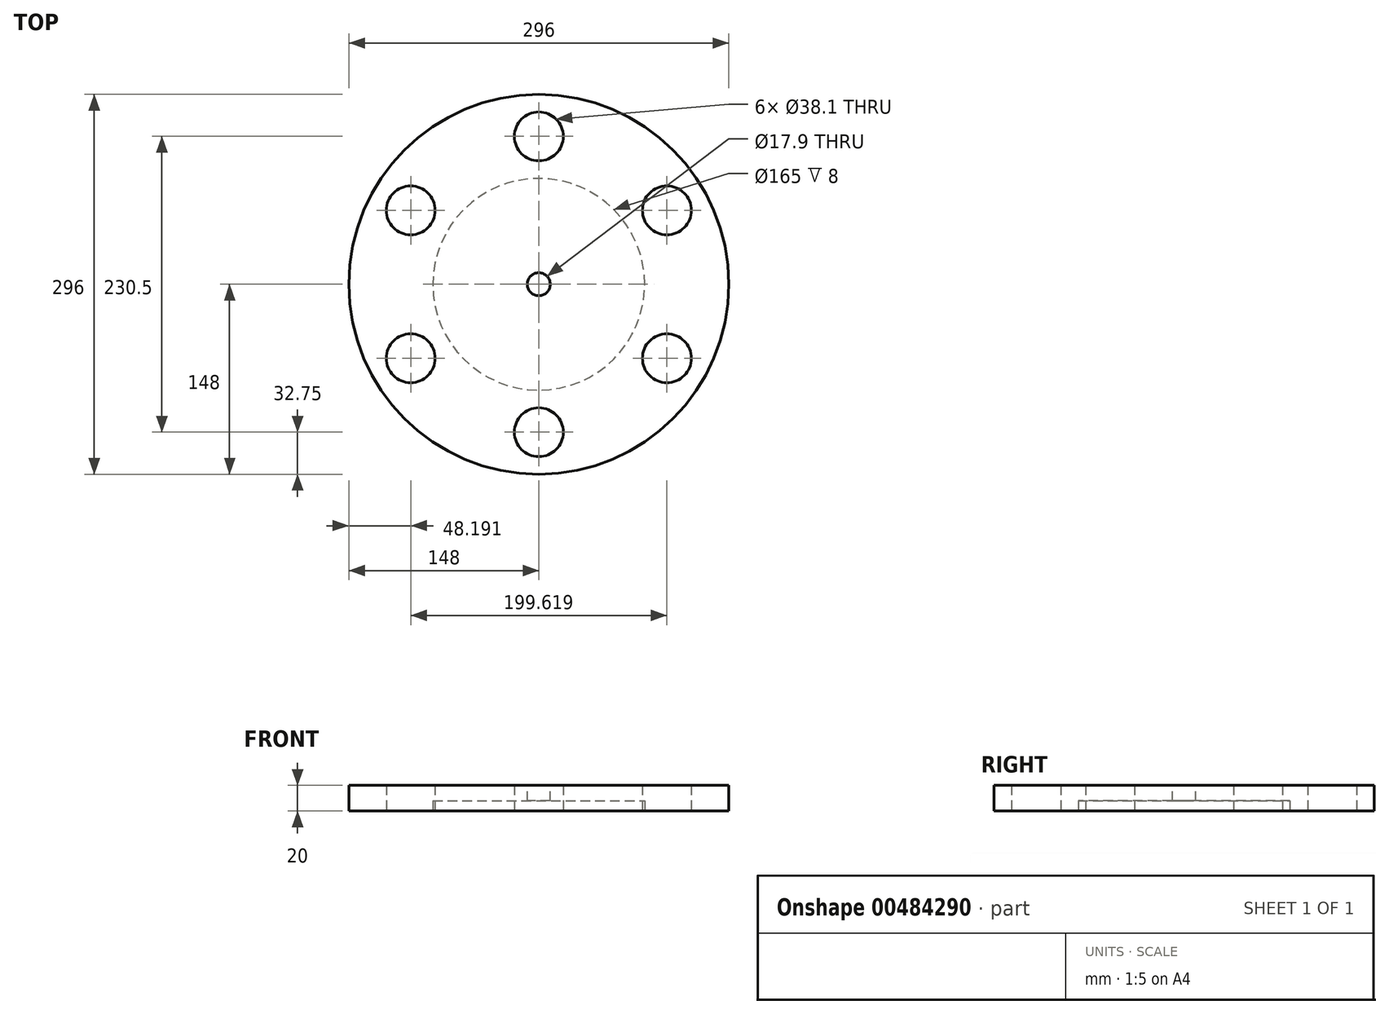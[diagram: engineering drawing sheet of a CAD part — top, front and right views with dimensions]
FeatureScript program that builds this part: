
annotation { "Feature Type Name" : "Feature", "Feature Type Description" : "" }
export const myFeature = defineFeature(function(context is Context, id is Id, definition is map)
    precondition{}
    {
        {
            var Q0;
            Q0=qCreatedBy(makeId("Top.planeOp"),FACE);
            var sketch = newSketch(context, id + "F0", { "sketchPlane" : qUnion([Q0])});
            skCircle(sketch, "E0", {"center": v(0, 0) * mm, "radius": 148 * mm});
            skCircle(sketch, "E1", {"center": v(0, 0) * mm, "radius": 8.95 * mm});
            skSolve(sketch);
        }
        {
            var Q0;
            Q0=makeQuery(id+"F0.imprint","IMPRINT",FACE,{"disambiguationData":[TD([[makeQuery(id+"F0.imprint","IMPRINT",EDGE,{"derivedFrom":sQuery(id+"F0.wireOp",EDGE,"E0")}),1.0]])]});
            extrude(context, id + "F1", {"entities" : qUnion([Q0]), "oppositeDirection" : true, "depth" : 20 * mm});
        }
        {
            var Q0;
            Q0=makeQuery(id+"F1.opExtrude","CAP_FACE",FACE,{"disambiguationData":[OSD([sQuery(id+"F0.wireOp",EDGE,"E0"),sQuery(id+"F0.wireOp",EDGE,"E1")])],"isStart":false});
            var sketch = newSketch(context, id + "F2", { "sketchPlane" : qUnion([Q0])});
            skCircle(sketch, "E2", {"center": v(0, 0) * mm, "radius": 82.5 * mm});
            skLineSegment(sketch, "E3", {"start": v(-82.5, 0) * mm, "end": v(-115.25, 0) * mm, "construction": true});
            skLineSegment(sketch, "E4", {"start": v(82.5, 0) * mm, "end": v(115.25, 0) * mm, "construction": true});
            skCircle(sketch, "E5", {"center": v(0, 0) * mm, "radius": 115.25 * mm, "construction": true});
            skLineSegment(sketch, "E6", {"start": v(0, 0) * mm, "end": v(0, 115.25) * mm, "construction": true});
            skLineSegment(sketch, "E7", {"start": v(0, 0) * mm, "end": v(99.8, 57.63) * mm, "construction": true});
            skLineSegment(sketch, "E8", {"start": v(0, 0) * mm, "end": v(99.8, -57.63) * mm, "construction": true});
            skLineSegment(sketch, "E9", {"start": v(0, 0) * mm, "end": v(0, -115.25) * mm, "construction": true});
            skLineSegment(sketch, "E10", {"start": v(0, 0) * mm, "end": v(-99.8, -57.63) * mm, "construction": true});
            skLineSegment(sketch, "E11", {"start": v(0, 0) * mm, "end": v(-99.8, 57.62) * mm, "construction": true});
            skCircle(sketch, "E12", {"center": v(-99.8, -57.63) * mm, "radius": 19.05 * mm});
            skCircle(sketch, "E13", {"center": v(0, -115.25) * mm, "radius": 19.05 * mm});
            skCircle(sketch, "E14", {"center": v(99.8, -57.62) * mm, "radius": 19.05 * mm});
            skCircle(sketch, "E15", {"center": v(99.8, 57.63) * mm, "radius": 19.05 * mm});
            skCircle(sketch, "E16", {"center": v(0, 115.25) * mm, "radius": 19.05 * mm});
            skCircle(sketch, "E17", {"center": v(-99.8, 57.62) * mm, "radius": 19.05 * mm});
            skSolve(sketch);
        }
        {
            var Q0;
            Q0=makeQuery(id+"F2.imprint","IMPRINT",FACE,{"disambiguationData":[TD([[makeQuery(id+"F2.imprint","IMPRINT",EDGE,{"derivedFrom":sQuery(id+"F2.wireOp",EDGE,"E2")}),1.0]])]});
            extrude(context, id + "F3", {"entities" : qUnion([Q0]), "operationType" : NewBodyOperationType.REMOVE, "oppositeDirection" : true, "depth" : 8 * mm});
        }
        {
            var Q0;
            Q0=makeQuery(id+"F2.imprint","IMPRINT",FACE,{"disambiguationData":[TD([[makeQuery(id+"F2.imprint","IMPRINT",EDGE,{"derivedFrom":sQuery(id+"F2.wireOp",EDGE,"E17")}),1.0]])]});
            var Q1;
            Q1=makeQuery(id+"F2.imprint","IMPRINT",FACE,{"disambiguationData":[TD([[makeQuery(id+"F2.imprint","IMPRINT",EDGE,{"derivedFrom":sQuery(id+"F2.wireOp",EDGE,"E12")}),1.0]])]});
            var Q2;
            Q2=makeQuery(id+"F2.imprint","IMPRINT",FACE,{"disambiguationData":[TD([[makeQuery(id+"F2.imprint","IMPRINT",EDGE,{"derivedFrom":sQuery(id+"F2.wireOp",EDGE,"E13")}),1.0]])]});
            var Q3;
            Q3=makeQuery(id+"F2.imprint","IMPRINT",FACE,{"disambiguationData":[TD([[makeQuery(id+"F2.imprint","IMPRINT",EDGE,{"derivedFrom":sQuery(id+"F2.wireOp",EDGE,"E14")}),1.0]])]});
            var Q4;
            Q4=makeQuery(id+"F2.imprint","IMPRINT",FACE,{"disambiguationData":[TD([[makeQuery(id+"F2.imprint","IMPRINT",EDGE,{"derivedFrom":sQuery(id+"F2.wireOp",EDGE,"E15")}),1.0]])]});
            var Q5;
            Q5=makeQuery(id+"F2.imprint","IMPRINT",FACE,{"disambiguationData":[TD([[makeQuery(id+"F2.imprint","IMPRINT",EDGE,{"derivedFrom":sQuery(id+"F2.wireOp",EDGE,"E16")}),1.0]])]});
            var Q6;
            Q6=makeQuery(id+"F1.opExtrude","CAP_FACE",FACE,{"disambiguationData":[OSD([sQuery(id+"F0.wireOp",EDGE,"E0"),sQuery(id+"F0.wireOp",EDGE,"E1")])],"isStart":true});
            extrude(context, id + "F4", {"entities" : qUnion([Q0, Q1, Q2, Q3, Q4, Q5]), "operationType" : NewBodyOperationType.REMOVE, "endBound" : BoundingType.UP_TO_SURFACE, "oppositeDirection" : true, "endBoundEntityFace" : qUnion([Q6]), "depth" : 10 * mm});
        }
        {
            var Q0;
            Q0=makeQuery(id+"F1.opExtrude","SWEPT_BODY",BODY,{"disambiguationData":[OSD([sQuery(id+"F0.wireOp",EDGE,"E0"),sQuery(id+"F0.wireOp",EDGE,"E1")])]});
            transform(context, id + "F5", {"entities" : qUnion([Q0]), "transformType" : TransformType.TRANSLATION_3D, "dx" : 0 * mm, "dy" : 0 * mm, "dz" : 0 * mm, "makeCopy" : true});
        }
        {
            var Q0;
            Q0=makeQuery(id+"F5.opPattern","COPY",BODY,{"derivedFrom":makeQuery(id+"F1.opExtrude","SWEPT_BODY",BODY,{"disambiguationData":[OSD([sQuery(id+"F0.wireOp",EDGE,"E0"),sQuery(id+"F0.wireOp",EDGE,"E1")])]}),"instanceName":"1"});
            deleteBodies(context, id + "F6", {"entities" : qUnion([Q0])});
        }
    });
